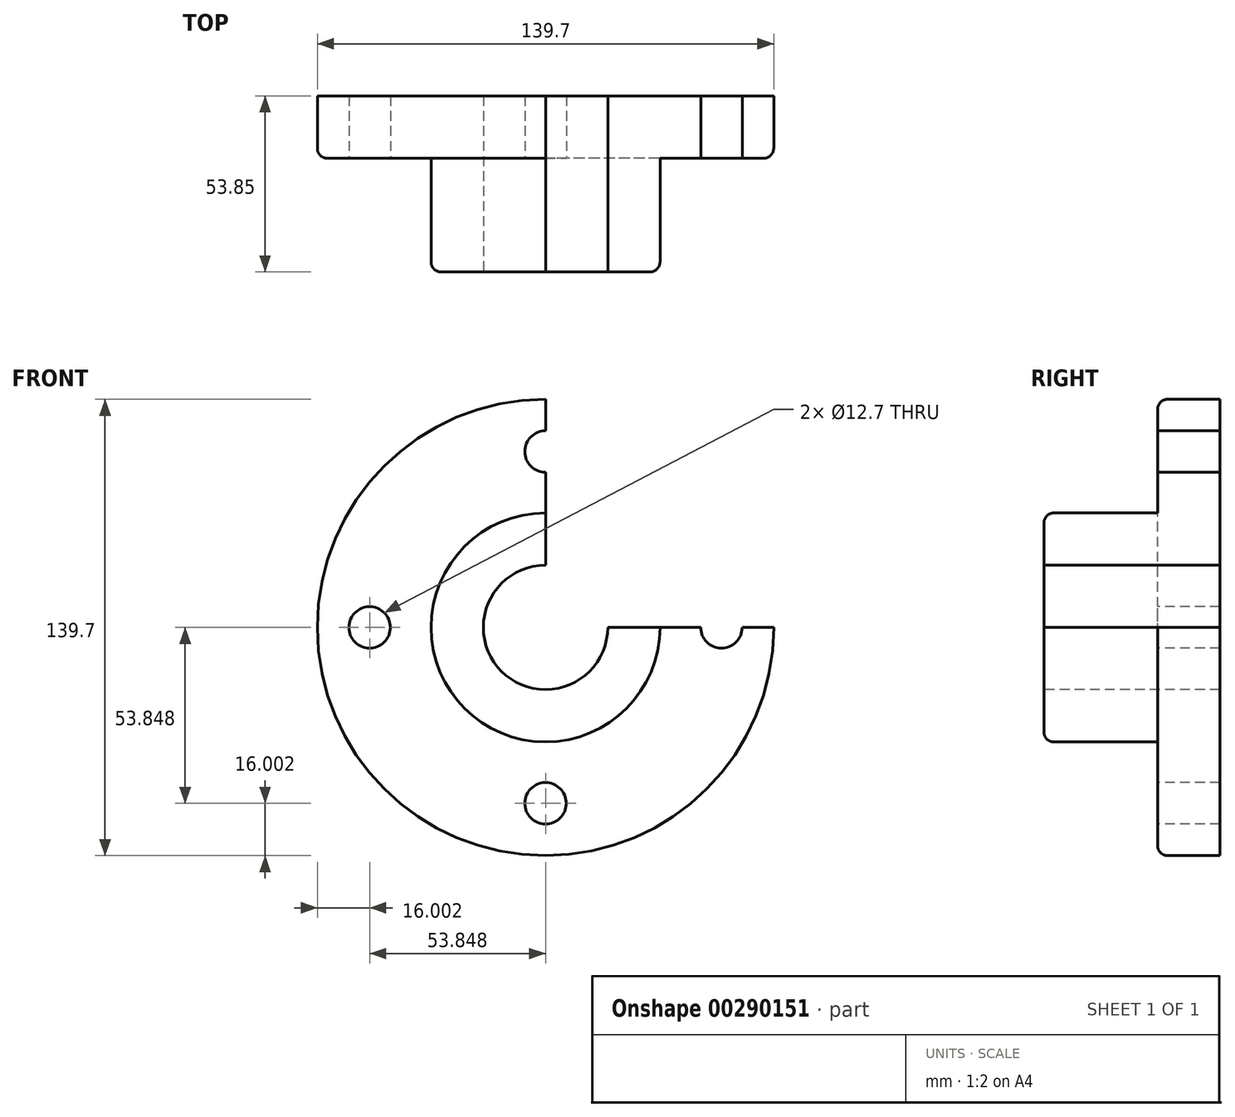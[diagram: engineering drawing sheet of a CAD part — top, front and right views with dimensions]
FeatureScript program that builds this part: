
annotation { "Feature Type Name" : "Feature", "Feature Type Description" : "" }
export const myFeature = defineFeature(function(context is Context, id is Id, definition is map)
    precondition{}
    {
        {
            var Q0;
            Q0=qCreatedBy(makeId("Right.planeOp"),FACE);
            var sketch = newSketch(context, id + "F0", { "sketchPlane" : qUnion([Q0])});
            skLineSegment(sketch, "E0.bottom", {"start": v(0, 0) * mm, "end": v(19.05, 0) * mm});
            skLineSegment(sketch, "E0.top", {"start": v(0, 69.85) * mm, "end": v(19.05, 69.85) * mm});
            skLineSegment(sketch, "E0.left", {"start": v(0, 0) * mm, "end": v(0, 69.85) * mm});
            skLineSegment(sketch, "E0.right", {"start": v(19.05, 0) * mm, "end": v(19.05, 69.85) * mm});
            skSolve(sketch);
        }
        {
            var Q0;
            Q0 = qSketchRegion(id + "F0", true);
            var Q1;
            Q1=sQuery(id+"F0.wireOp",EDGE,"E0.bottom");
            revolve(context, id + "F1", {"entities" : qUnion([Q0]), "axis" : qUnion([Q1]), "revolveType" : RevolveType.ONE_DIRECTION, "oppositeDirection" : true, "angle" : 270 * degree});
        }
        {
            var Q0;
            Q0=makeQuery(id+"F1.opRevolve","SWEPT_EDGE",EDGE,{"disambiguationData":[OSD([sQuery(id+"F0.wireOp",EDGE,"E0.top"),sQuery(id+"F0.wireOp",EDGE,"E0.left")])]});
            fillet(context, id + "F2", {"entities" : qUnion([Q0]), "radius" : 3.05 * mm, "tangentPropagation" : true, "allowEdgeOverflow" : false});
        }
        {
            var Q0;
            Q0=qCreatedBy(makeId("Right.planeOp"),FACE);
            var sketch = newSketch(context, id + "F3", { "sketchPlane" : qUnion([Q0])});
            skLineSegment(sketch, "E1.bottom", {"start": v(0, 0) * mm, "end": v(-34.8, 0) * mm});
            skLineSegment(sketch, "E1.top", {"start": v(0, 35.05) * mm, "end": v(-34.8, 35.05) * mm});
            skLineSegment(sketch, "E1.left", {"start": v(0, 0) * mm, "end": v(0, 35.05) * mm});
            skLineSegment(sketch, "E1.right", {"start": v(-34.8, 0) * mm, "end": v(-34.8, 35.05) * mm});
            skSolve(sketch);
        }
        {
            var Q0;
            Q0=makeQuery(id+"F3.imprint","IMPRINT",FACE,{"disambiguationData":[TD([[makeQuery(id+"F3.imprint","IMPRINT",EDGE,{"derivedFrom":sQuery(id+"F3.wireOp",EDGE,"E1.bottom")}),-1.0]])]});
            var Q1;
            Q1=sQuery(id+"F3.wireOp",EDGE,"E1.bottom");
            revolve(context, id + "F4", {"operationType" : NewBodyOperationType.ADD, "entities" : qUnion([Q0]), "axis" : qUnion([Q1]), "revolveType" : RevolveType.ONE_DIRECTION, "angle" : 270 * degree});
        }
        {
            var Q0;
            Q0=makeQuery(id+"F4.opRevolve","SWEPT_EDGE",EDGE,{"disambiguationData":[OSD([sQuery(id+"F3.wireOp",EDGE,"E1.top"),sQuery(id+"F3.wireOp",EDGE,"E1.right")])]});
            var Q1;
            Q1=makeQuery(id+"F4.opRevolve","SWEPT_EDGE",EDGE,{"disambiguationData":[OSD([sQuery(id+"F3.wireOp",EDGE,"E1.top"),sQuery(id+"F3.wireOp",EDGE,"E1.left")])]});
            fillet(context, id + "F5", {"entities" : qUnion([Q0, Q1]), "radius" : 3.05 * mm, "tangentPropagation" : true, "allowEdgeOverflow" : false});
        }
        {
            var Q0;
            Q0=makeQuery(id+"F4.opRevolve","SWEPT_FACE",FACE,{"disambiguationData":[OSD([sQuery(id+"F3.wireOp",EDGE,"E1.right")])]});
            var sketch = newSketch(context, id + "F6", { "sketchPlane" : qUnion([Q0])});
            skCircle(sketch, "E2", {"center": v(0, 0) * mm, "radius": 19.05 * mm});
            skSolve(sketch);
        }
        {
            var Q0;
            Q0 = qSketchRegion(id + "F6", true);
            extrude(context, id + "F7", {"entities" : qUnion([Q0]), "operationType" : NewBodyOperationType.REMOVE, "endBound" : BoundingType.THROUGH_ALL, "oppositeDirection" : true, "depth" : 25.4 * mm});
        }
        {
            var Q0;
            Q0=qCreatedBy(makeId("Front.planeOp"),FACE);
            var sketch = newSketch(context, id + "F8", { "sketchPlane" : qUnion([Q0])});
            skCircle(sketch, "E3", {"center": v(0, 53.85) * mm, "radius": 6.35 * mm});
            skCircle(sketch, "E4.1.0", {"center": v(-53.85, 0) * mm, "radius": 6.35 * mm});
            skCircle(sketch, "E4.2.0", {"center": v(0, -53.85) * mm, "radius": 6.35 * mm});
            skCircle(sketch, "E4.3.0", {"center": v(53.85, 0) * mm, "radius": 6.35 * mm});
            skPoint(sketch, "E4.center", {"position": v(0, 0) * mm});
            skSolve(sketch);
        }
        {
            var Q0;
            Q0 = qSketchRegion(id + "F8", true);
            extrude(context, id + "F9", {"entities" : qUnion([Q0]), "operationType" : NewBodyOperationType.REMOVE, "endBound" : BoundingType.THROUGH_ALL, "oppositeDirection" : true, "depth" : 25.4 * mm});
        }
    });
